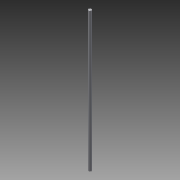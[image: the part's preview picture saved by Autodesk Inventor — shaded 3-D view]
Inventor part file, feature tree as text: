
AUTODESK INVENTOR PART (.ipt)
format: ipt  version: 2014 SP1 (Build 180222100, 222)  size: 70,144 bytes
history: native  units: in
note: dims shown in document units (in); Inventor stores cm internally (conversion verified against a paired STEP export)
features: extrude x1, sketch x1
ambient origin geometry x8: Origin, YZ Plane, XZ Plane, XY Plane, X Axis, Y Axis, Z Axis, Center Point
bodies: Solid1 (feature_tree)
feature tree (2):
  extrude  "Extrusion1"  Depth=19.0in TaperAngle=0.0deg
  sketch  "Sketch1"  dims[d0=0.375in d1=19.0in d2=0.0in]
